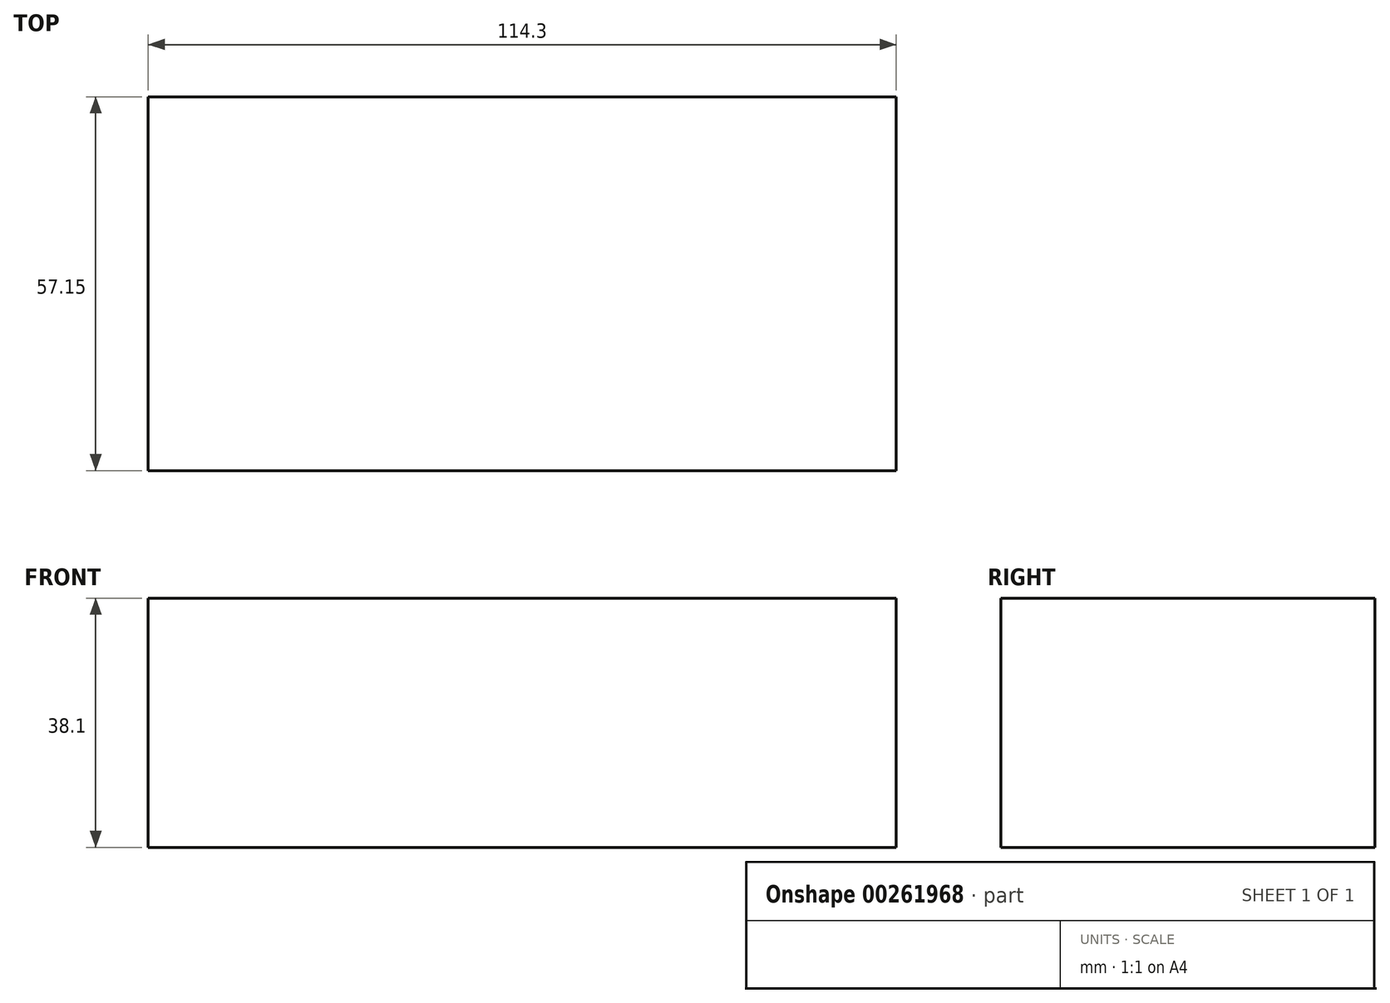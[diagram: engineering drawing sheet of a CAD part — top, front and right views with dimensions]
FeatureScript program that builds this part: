
annotation { "Feature Type Name" : "Feature", "Feature Type Description" : "" }
export const myFeature = defineFeature(function(context is Context, id is Id, definition is map)
    precondition{}
    {
        {
            var Q0;
            Q0=qCreatedBy(makeId("Front.planeOp"),FACE);
            var sketch = newSketch(context, id + "F0", { "sketchPlane" : qUnion([Q0])});
            skLineSegment(sketch, "E0.bottom", {"start": v(0, 0) * mm, "end": v(114.3, 0) * mm});
            skLineSegment(sketch, "E0.top", {"start": v(0, -38.1) * mm, "end": v(114.3, -38.1) * mm});
            skLineSegment(sketch, "E0.left", {"start": v(0, 0) * mm, "end": v(0, -38.1) * mm});
            skLineSegment(sketch, "E0.right", {"start": v(114.3, 0) * mm, "end": v(114.3, -38.1) * mm});
            skSolve(sketch);
        }
        {
            var Q0;
            Q0 = qSketchRegion(id + "F0", true);
            extrude(context, id + "F1", {"entities" : qUnion([Q0]), "depth" : 57.15 * mm});
        }
    });
